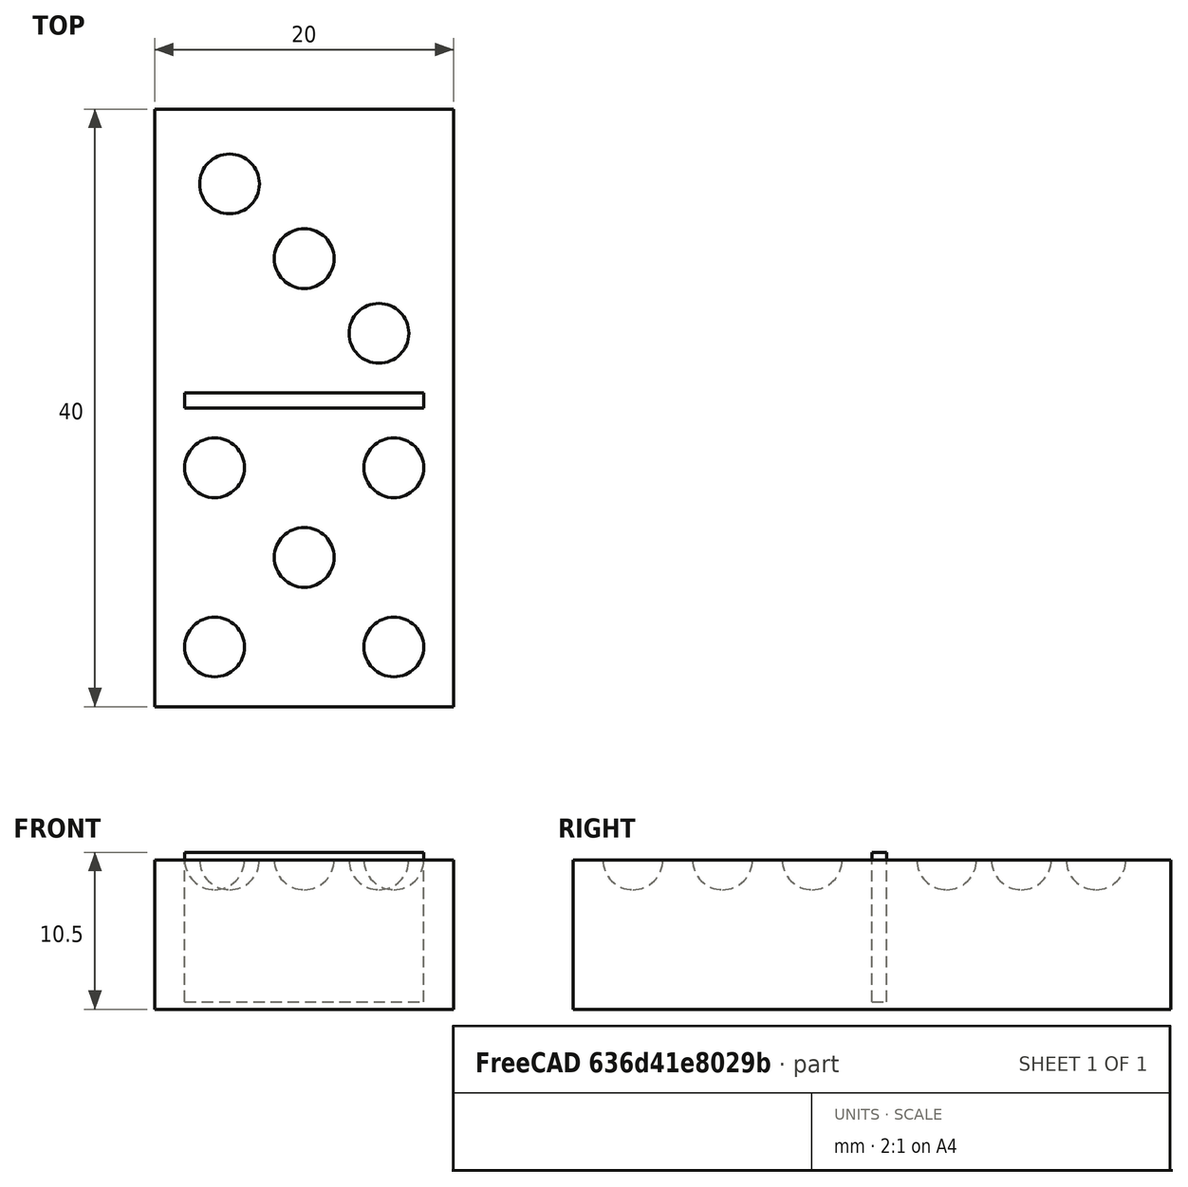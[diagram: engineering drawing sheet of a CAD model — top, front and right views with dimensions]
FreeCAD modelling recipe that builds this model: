
FCSTD DOCUMENT  (FreeCAD 1.0R39319 (Git))
Label: ojt1_t13r03_domino
License: All rights reserved
LicenseURL: https://en.wikipedia.org/wiki/All_rights_reserved
objects: Part::Sphere×8, Part::Box×2, Part::MultiFuse×2, Part::Cut×2
note: 14 computed .brp shape members not serialized (recipe doc carries the construction recipe); baked Part::Feature solids carry a one-line shape summary decoded from their .brp

FEATURE [Part::Box] Box  label="Cub"
  AttacherType = Attacher::AttachEngine3D
  Height = 10
  Length = 20
  Width = 40
FEATURE [Part::Box] Box001  label="Cub001"
  AttacherType = Attacher::AttachEngine3D
  Height = 10
  Length = 16
  Placement = pos=(2,20,0.5) rot=(0,0,1;0rad)
  Width = 1
FEATURE [Part::Sphere] Sphere  label="Esfera"
  Angle1 = -90
  Angle2 = 90
  Angle3 = 360
  AttacherType = Attacher::AttachEngine3D
  Placement = pos=(4,4,10) rot=(0,0,1;0rad)
  Radius = 2
FEATURE [Part::Sphere] Sphere001  label="Esfera001"
  Angle1 = -90
  Angle2 = 90
  Angle3 = 360
  AttacherType = Attacher::AttachEngine3D
  Placement = pos=(16,4,10) rot=(0,0,1;0rad)
  Radius = 2
FEATURE [Part::Sphere] Sphere002  label="Esfera002"
  Angle1 = -90
  Angle2 = 90
  Angle3 = 360
  AttacherType = Attacher::AttachEngine3D
  Placement = pos=(4,16,10) rot=(0,0,1;0rad)
  Radius = 2
FEATURE [Part::Sphere] Sphere003  label="Esfera003"
  Angle1 = -90
  Angle2 = 90
  Angle3 = 360
  AttacherType = Attacher::AttachEngine3D
  Placement = pos=(16,16,10) rot=(0,0,1;0rad)
  Radius = 2
FEATURE [Part::Sphere] Sphere004  label="Esfera004"
  Angle1 = -90
  Angle2 = 90
  Angle3 = 360
  AttacherType = Attacher::AttachEngine3D
  Placement = pos=(10,10,10) rot=(0,0,1;0rad)
  Radius = 2
FEATURE [Part::MultiFuse] Fusion  label="5"
  Refine = true
  Shapes = -> [Sphere,Sphere001,Sphere002,Sphere003,Sphere004]
FEATURE [Part::Sphere] Sphere005  label="Esfera005"
  Angle1 = -90
  Angle2 = 90
  Angle3 = 360
  AttacherType = Attacher::AttachEngine3D
  Placement = pos=(5,35,10) rot=(0,0,1;0rad)
  Radius = 2
FEATURE [Part::Sphere] Sphere006  label="Esfera006"
  Angle1 = -90
  Angle2 = 90
  Angle3 = 360
  AttacherType = Attacher::AttachEngine3D
  Placement = pos=(15,25,10) rot=(0,0,1;0rad)
  Radius = 2
FEATURE [Part::Sphere] Sphere007  label="Esfera007"
  Angle1 = -90
  Angle2 = 90
  Angle3 = 360
  AttacherType = Attacher::AttachEngine3D
  Placement = pos=(10,30,10) rot=(0,0,1;0rad)
  Radius = 2
FEATURE [Part::MultiFuse] Fusion001  label="3"
  Refine = true
  Shapes = -> [Sphere005,Sphere006,Sphere007]
FEATURE [Part::Cut] Cut
  Base = -> Box
  Refine = true
  Tool = -> Fusion
FEATURE [Part::Cut] Cut001
  Base = -> Cut
  Refine = true
  Tool = -> Fusion001
